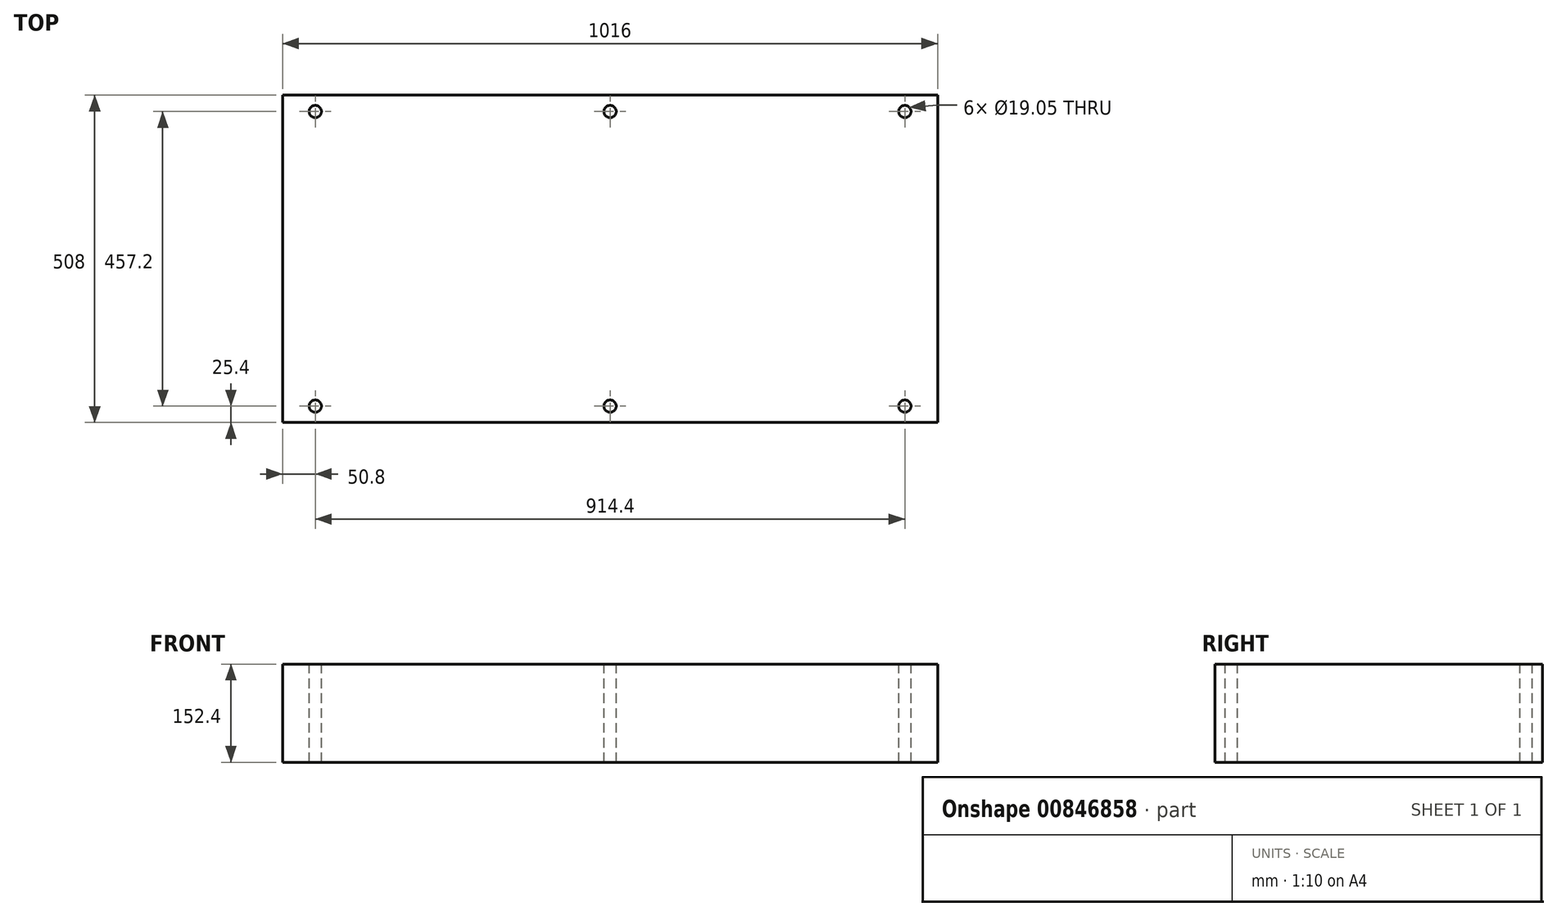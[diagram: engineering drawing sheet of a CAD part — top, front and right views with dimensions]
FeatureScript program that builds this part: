
annotation { "Feature Type Name" : "Feature", "Feature Type Description" : "" }
export const myFeature = defineFeature(function(context is Context, id is Id, definition is map)
    precondition{}
    {
        {
            var Q0;
            Q0=qCreatedBy(makeId("Top.planeOp"),FACE);
            var sketch = newSketch(context, id + "F0", { "sketchPlane" : qUnion([Q0])});
            skLineSegment(sketch, "E0.bottom", {"start": v(-508, 254) * mm, "end": v(508, 254) * mm});
            skLineSegment(sketch, "E0.top", {"start": v(-508, -254) * mm, "end": v(508, -254) * mm});
            skLineSegment(sketch, "E0.left", {"start": v(-508, 254) * mm, "end": v(-508, -254) * mm});
            skLineSegment(sketch, "E0.right", {"start": v(508, 254) * mm, "end": v(508, -254) * mm});
            skLineSegment(sketch, "E1", {"start": v(-508, -254) * mm, "end": v(508, 254) * mm, "construction": true});
            skSolve(sketch);
        }
        {
            var Q0;
            Q0 = qSketchRegion(id + "F0", true);
            extrude(context, id + "F1", {"entities" : qUnion([Q0]), "flatOperationType" : FlatOperationType.REMOVE, "depth" : 152.4 * mm, "offsetDistance" : 25.4 * mm, "domain" : OperationDomain.MODEL});
        }
        {
            var Q0;
            Q0=makeQuery(id+"F1.opExtrude","CAP_FACE",FACE,{"disambiguationData":[OSD([sQuery(id+"F0.wireOp",EDGE,"E0.bottom"),sQuery(id+"F0.wireOp",EDGE,"E0.top"),sQuery(id+"F0.wireOp",EDGE,"E0.left"),sQuery(id+"F0.wireOp",EDGE,"E0.right")])],"isStart":false});
            var sketch = newSketch(context, id + "F2", { "sketchPlane" : qUnion([Q0])});
            skLineSegment(sketch, "E2.bottom", {"start": v(-457.2, 228.6) * mm, "end": v(457.2, 228.6) * mm, "construction": true});
            skLineSegment(sketch, "E2.top", {"start": v(-457.2, -228.6) * mm, "end": v(457.2, -228.6) * mm, "construction": true});
            skLineSegment(sketch, "E2.left", {"start": v(-457.2, 228.6) * mm, "end": v(-457.2, -228.6) * mm, "construction": true});
            skLineSegment(sketch, "E2.right", {"start": v(457.2, 228.6) * mm, "end": v(457.2, -228.6) * mm, "construction": true});
            skLineSegment(sketch, "E3", {"start": v(-457.2, -228.6) * mm, "end": v(457.2, 228.6) * mm, "construction": true});
            skCircle(sketch, "E4", {"center": v(-457.2, 228.6) * mm, "radius": 9.53 * mm});
            skCircle(sketch, "E5", {"center": v(457.2, 228.6) * mm, "radius": 9.53 * mm});
            skCircle(sketch, "E6", {"center": v(-457.2, -228.6) * mm, "radius": 9.53 * mm});
            skCircle(sketch, "E7", {"center": v(457.2, -228.6) * mm, "radius": 9.53 * mm});
            skCircle(sketch, "E8", {"center": v(0, -228.6) * mm, "radius": 9.53 * mm});
            skCircle(sketch, "E9", {"center": v(0, 228.6) * mm, "radius": 9.53 * mm});
            skSolve(sketch);
        }
        {
            var Q0;
            Q0 = qSketchRegion(id + "F2", true);
            var Q1;
            Q1=sQuery(id+"F2.wireOp",EDGE,"E3");
            var Q2;
            Q2=sQuery(id+"F2.wireOp",EDGE,"E2.left");
            var Q3;
            Q3=sQuery(id+"F2.wireOp",EDGE,"E2.bottom");
            var Q4;
            Q4=sQuery(id+"F2.wireOp",EDGE,"E2.top");
            var Q5;
            Q5=sQuery(id+"F2.wireOp",EDGE,"E2.right");
            extrude(context, id + "F3", {"entities" : qUnion([Q0]), "operationType" : NewBodyOperationType.REMOVE, "surfaceEntities" : qUnion([Q1, Q2, Q3, Q4, Q5]), "endBound" : BoundingType.UP_TO_NEXT, "oppositeDirection" : true, "depth" : 25.4 * mm, "offsetDistance" : 25.4 * mm});
        }
    });
